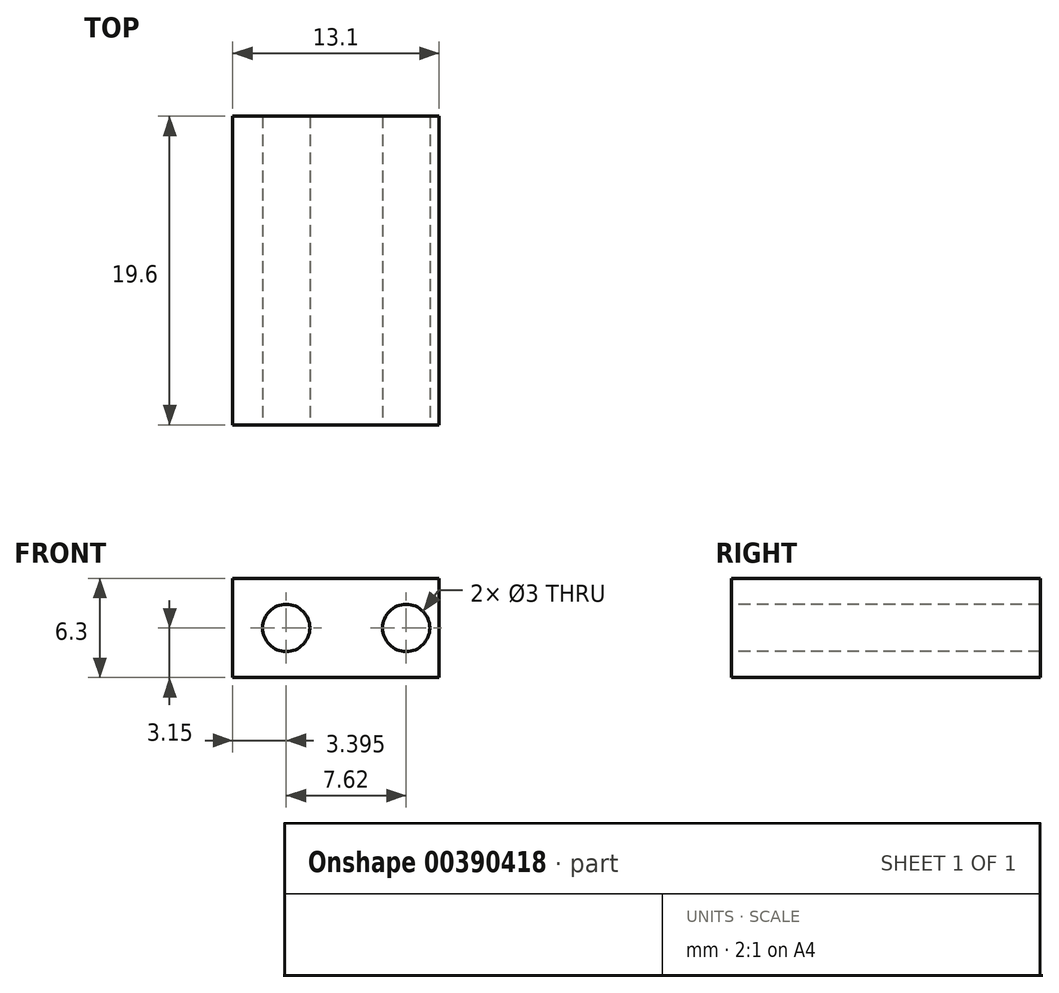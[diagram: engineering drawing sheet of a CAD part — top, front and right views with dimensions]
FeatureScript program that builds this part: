
annotation { "Feature Type Name" : "Feature", "Feature Type Description" : "" }
export const myFeature = defineFeature(function(context is Context, id is Id, definition is map)
    precondition{}
    {
        {
            var Q0;
            Q0=qCreatedBy(makeId("Front.planeOp"),FACE);
            var sketch = newSketch(context, id + "F0", { "sketchPlane" : qUnion([Q0])});
            skLineSegment(sketch, "E0.bottom", {"start": v(6.55, 3.15) * mm, "end": v(-6.55, 3.15) * mm});
            skLineSegment(sketch, "E0.top", {"start": v(6.55, -3.15) * mm, "end": v(-6.55, -3.15) * mm});
            skLineSegment(sketch, "E0.left", {"start": v(6.55, 3.15) * mm, "end": v(6.55, -3.15) * mm});
            skLineSegment(sketch, "E0.right", {"start": v(-6.55, 3.15) * mm, "end": v(-6.55, -3.15) * mm});
            skPoint(sketch, "E0.middle", {"position": v(0, 0) * mm});
            skSolve(sketch);
        }
        {
            var Q0;
            Q0 = qSketchRegion(id + "F0", true);
            extrude(context, id + "F1", {"entities" : qUnion([Q0]), "depth" : 19.6 * mm});
        }
        {
            var Q0;
            Q0=makeQuery(id+"F1.opExtrude","CAP_FACE",FACE,{"disambiguationData":[OSD([sQuery(id+"F0.wireOp",EDGE,"E0.bottom"),sQuery(id+"F0.wireOp",EDGE,"E0.top"),sQuery(id+"F0.wireOp",EDGE,"E0.left"),sQuery(id+"F0.wireOp",EDGE,"E0.right")])],"isStart":false});
            var sketch = newSketch(context, id + "F2", { "sketchPlane" : qUnion([Q0])});
            skCircle(sketch, "E1", {"center": v(-3.15, 0) * mm, "radius": 1.5 * mm});
            skCircle(sketch, "E2", {"center": v(4.47, 0) * mm, "radius": 1.5 * mm});
            skSolve(sketch);
        }
        {
            var Q0;
            Q0=makeQuery(id+"F2.imprint","IMPRINT",FACE,{"disambiguationData":[TD([[makeQuery(id+"F2.imprint","IMPRINT",EDGE,{"derivedFrom":sQuery(id+"F2.wireOp",EDGE,"E1")}),1.0]])]});
            var Q1;
            Q1=makeQuery(id+"F2.imprint","IMPRINT",FACE,{"disambiguationData":[TD([[makeQuery(id+"F2.imprint","IMPRINT",EDGE,{"derivedFrom":sQuery(id+"F2.wireOp",EDGE,"E2")}),1.0]])]});
            extrude(context, id + "F3", {"entities" : qUnion([Q0, Q1]), "operationType" : NewBodyOperationType.REMOVE, "oppositeDirection" : true, "depth" : 25 * mm});
        }
    });
